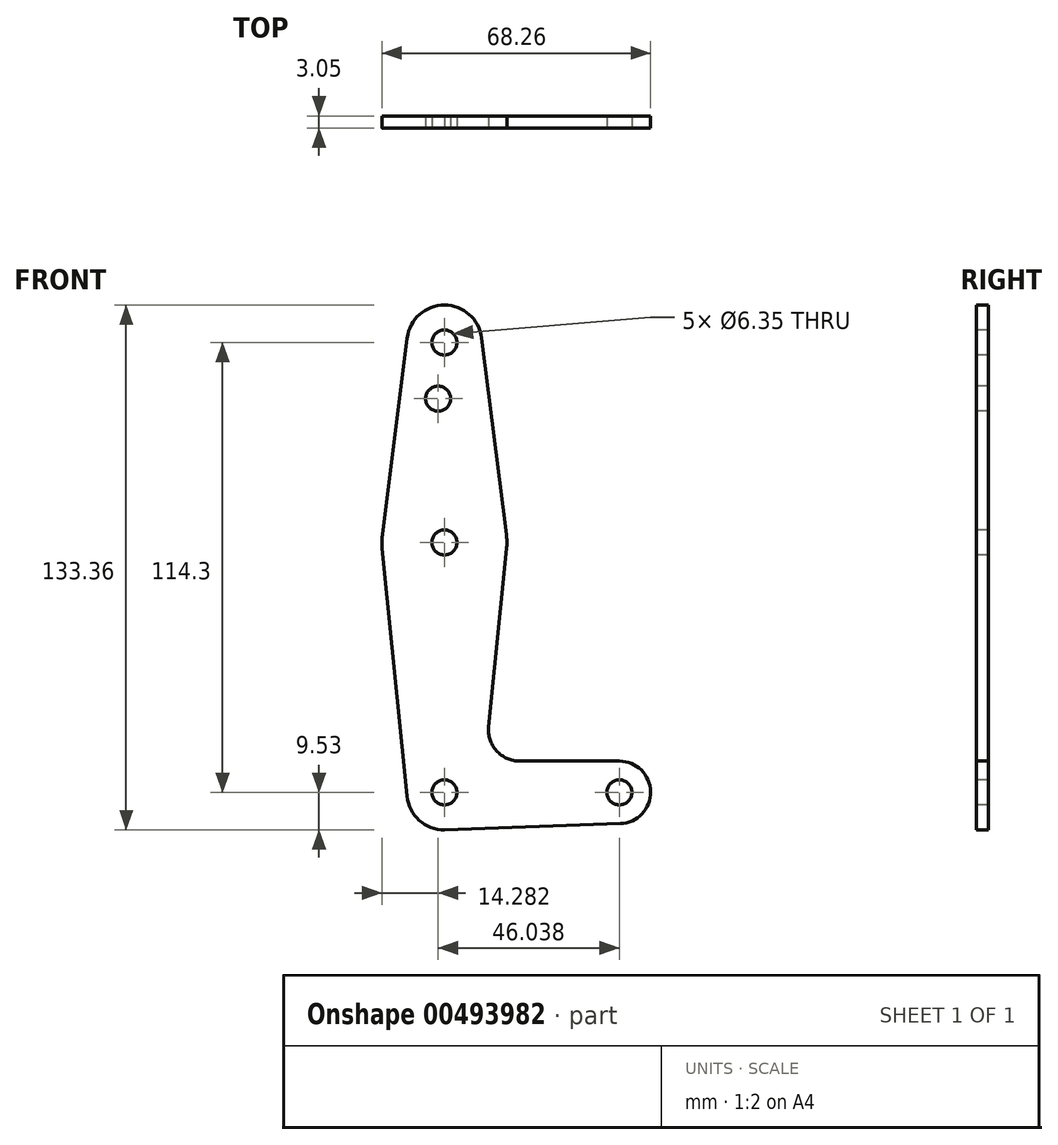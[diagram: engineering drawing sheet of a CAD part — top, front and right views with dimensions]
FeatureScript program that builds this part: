
annotation { "Feature Type Name" : "Feature", "Feature Type Description" : "" }
export const myFeature = defineFeature(function(context is Context, id is Id, definition is map)
    precondition{}
    {
        {
            var Q0;
            Q0=qCreatedBy(makeId("Front.planeOp"),FACE);
            var sketch = newSketch(context, id + "F0", { "sketchPlane" : qUnion([Q0])});
            skLineSegment(sketch, "E0", {"start": v(0, 0) * mm, "end": v(0, 114.3) * mm, "construction": true});
            skLineSegment(sketch, "E1", {"start": v(0, 0) * mm, "end": v(44.45, 0) * mm, "construction": true});
            skCircle(sketch, "E2", {"center": v(0, 114.3) * mm, "radius": 9.53 * mm});
            skCircle(sketch, "E3", {"center": v(44.45, 0) * mm, "radius": 7.94 * mm});
            skCircle(sketch, "E4", {"center": v(0, 0) * mm, "radius": 9.53 * mm});
            skCircle(sketch, "E5", {"center": v(0, 63.5) * mm, "radius": 15.88 * mm});
            skLineSegment(sketch, "E6", {"start": v(-9.45, 115.5) * mm, "end": v(-15.75, 65.48) * mm});
            skLineSegment(sketch, "E7", {"start": v(9.45, 115.5) * mm, "end": v(15.75, 65.48) * mm});
            skLineSegment(sketch, "E8", {"start": v(-15.8, 61.91) * mm, "end": v(-9.48, -0.95) * mm});
            skLineSegment(sketch, "E9", {"start": v(0, -9.53) * mm, "end": v(44.73, -7.93) * mm});
            skCircle(sketch, "E10", {"center": v(0, 114.3) * mm, "radius": 3.18 * mm});
            skCircle(sketch, "E11", {"center": v(0, 63.5) * mm, "radius": 3.18 * mm});
            skCircle(sketch, "E12", {"center": v(0, 0) * mm, "radius": 3.18 * mm});
            skCircle(sketch, "E13", {"center": v(44.45, 0) * mm, "radius": 3.18 * mm});
            skCircle(sketch, "E14", {"center": v(-1.59, 100.03) * mm, "radius": 3.18 * mm});
            skLineSegment(sketch, "E15", {"start": v(15.8, 61.91) * mm, "end": v(11.25, 16.68) * mm});
            skLineSegment(sketch, "E16", {"start": v(19.16, 7.94) * mm, "end": v(44.45, 7.94) * mm});
            skArc(sketch, "E17.filletArc", {"start": v(11.25, 16.68) * mm, "mid": v(13.26, 10.55) * mm, "end": v(19.16, 7.94) * mm});
            skSolve(sketch);
        }
        {
            var Q0;
            Q0=makeQuery(id+"F0.imprint","IMPRINT",FACE,{"disambiguationData":[TD([[makeQuery(id+"F0.imprint","IMPRINT",EDGE,{"derivedFrom":sQuery(id+"F0.wireOp",EDGE,"E11")}),-1.0]])]});
            var Q1;
            {var subQ1=sQuery(id+"F0.wireOp",EDGE,"E6");Q1=makeQuery(id+"F0.imprint","IMPRINT",FACE,{"disambiguationData":[TD([[makeQuery(id+"F0.imprint","IMPRINT",EDGE,{"derivedFrom":subQ1}),1.0]])]});}
            var Q2;
            Q2=makeQuery(id+"F0.imprint","IMPRINT",FACE,{"disambiguationData":[TD([[makeQuery(id+"F0.imprint","IMPRINT",EDGE,{"derivedFrom":sQuery(id+"F0.wireOp",EDGE,"E10")}),-1.0]])]});
            var Q3;
            {var subQ0=sQuery(id+"F0.wireOp",EDGE,"E8");Q3=makeQuery(id+"F0.imprint","IMPRINT",FACE,{"disambiguationData":[TD([[makeQuery(id+"F0.imprint","IMPRINT",EDGE,{"derivedFrom":subQ0}),1.0]])]});}
            var Q4;
            Q4=makeQuery(id+"F0.imprint","IMPRINT",FACE,{"disambiguationData":[TD([[makeQuery(id+"F0.imprint","IMPRINT",EDGE,{"derivedFrom":sQuery(id+"F0.wireOp",EDGE,"E12")}),-1.0]])]});
            var Q5;
            Q5=makeQuery(id+"F0.imprint","IMPRINT",FACE,{"disambiguationData":[TD([[makeQuery(id+"F0.imprint","IMPRINT",EDGE,{"derivedFrom":sQuery(id+"F0.wireOp",EDGE,"E13")}),-1.0]])]});
            extrude(context, id + "F1", {"entities" : qUnion([Q0, Q1, Q2, Q3, Q4, Q5]), "oppositeDirection" : true, "depth" : 3.05 * mm});
        }
    });
